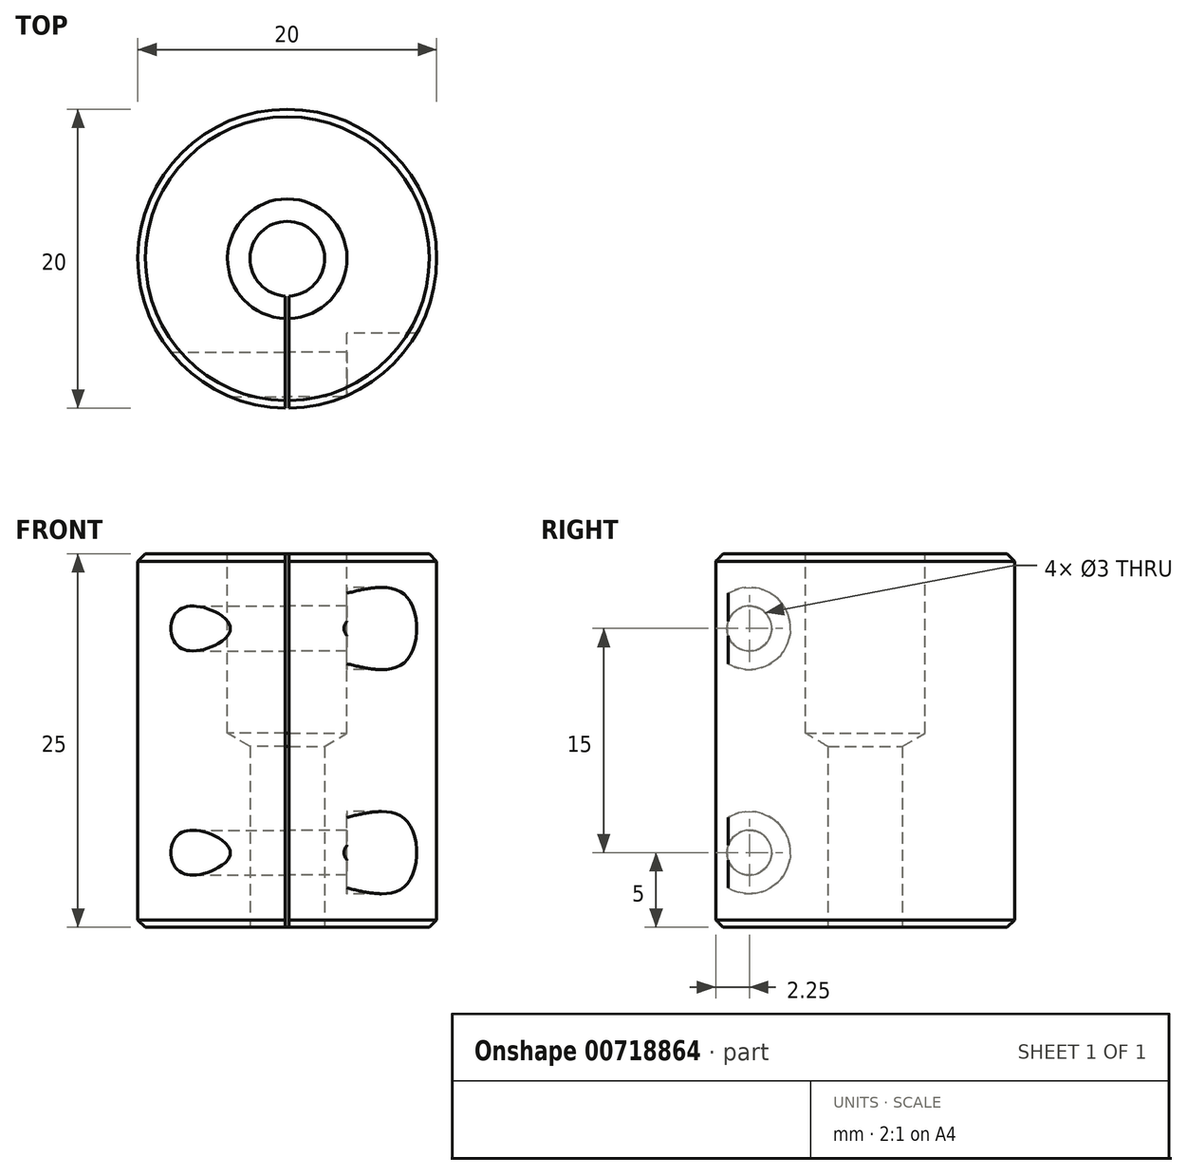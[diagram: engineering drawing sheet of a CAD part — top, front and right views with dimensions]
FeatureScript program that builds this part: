
annotation { "Feature Type Name" : "Feature", "Feature Type Description" : "" }
export const myFeature = defineFeature(function(context is Context, id is Id, definition is map)
    precondition{}
    {
        {
            var Q0;
            Q0=qCreatedBy(makeId("Top.planeOp"),FACE);
            var sketch = newSketch(context, id + "F0", { "sketchPlane" : qUnion([Q0])});
            skCircle(sketch, "E0", {"center": v(0, 0) * mm, "radius": 10 * mm});
            skSolve(sketch);
        }
        {
            var Q0;
            Q0=makeQuery(id+"F0.imprint","IMPRINT",FACE,{"disambiguationData":[TD([[makeQuery(id+"F0.imprint","IMPRINT",EDGE,{"derivedFrom":sQuery(id+"F0.wireOp",EDGE,"E0")}),1.0]])]});
            extrude(context, id + "F1", {"entities" : qUnion([Q0]), "oppositeDirection" : true, "depth" : 25 * mm, "offsetDistance" : 25 * mm});
        }
        {
            var Q0;
            Q0=sQuery(id+"F0.wireOp",VERTEX,"E0.center");
            var Q1;
            Q1=makeQuery(id+"F1.opExtrude","SWEPT_BODY",BODY,{"disambiguationData":[OSD([sQuery(id+"F0.wireOp",EDGE,"E0")])]});
            hole(context, id + "F2", {"style" : HoleStyle.SIMPLE, "endStyle" : HoleEndStyle.BLIND, "holeDiameter" : 8 * mm, "majorDiameter" : 5 * mm, "holeDepth" : 12 * mm, "isTappedThrough" : true, "tappedDepth" : 12 * mm, "tapClearance" : 3, "locations" : qUnion([Q0]), "scope" : qUnion([Q1])});
        }
        {
            var Q0;
            Q0=makeQuery(id+"F1.opExtrude","CAP_FACE",FACE,{"disambiguationData":[OSD([sQuery(id+"F0.wireOp",EDGE,"E0")])],"isStart":false});
            var sketch = newSketch(context, id + "F3", { "sketchPlane" : qUnion([Q0])});
            skCircle(sketch, "E1", {"center": v(0, 0) * mm, "radius": 2.5 * mm});
            skSolve(sketch);
        }
        {
            var Q0;
            Q0 = qSketchRegion(id + "F3", true);
            extrude(context, id + "F4", {"entities" : qUnion([Q0]), "operationType" : NewBodyOperationType.REMOVE, "oppositeDirection" : true, "depth" : 25 * mm, "offsetDistance" : 25 * mm});
        }
        {
            var Q0;
            Q0=qCreatedBy(makeId("Top.planeOp"),FACE);
            var sketch = newSketch(context, id + "F5", { "sketchPlane" : qUnion([Q0])});
            skLineSegment(sketch, "E2.bottom", {"start": v(-0.13, 0) * mm, "end": v(0.13, 0) * mm});
            skLineSegment(sketch, "E2.top", {"start": v(-0.12, -12) * mm, "end": v(0.12, -12) * mm});
            skLineSegment(sketch, "E2.left", {"start": v(-0.13, 0) * mm, "end": v(-0.12, -12) * mm});
            skLineSegment(sketch, "E2.right", {"start": v(0.13, 0) * mm, "end": v(0.12, -12) * mm});
            skSolve(sketch);
        }
        {
            var Q0;
            Q0 = qSketchRegion(id + "F5", true);
            extrude(context, id + "F6", {"entities" : qUnion([Q0]), "operationType" : NewBodyOperationType.REMOVE, "endBound" : BoundingType.THROUGH_ALL, "oppositeDirection" : true, "depth" : 25 * mm, "offsetDistance" : 25 * mm});
        }
        {
            var Q0;
            Q0=makeQuery(id+"F4.boolean.opBoolean","COPY",EDGE,{"derivedFrom":makeQuery(id+"F4.opExtrude","CAP_EDGE",EDGE,{"disambiguationData":[OSD([sQuery(id+"F3.wireOp",EDGE,"E1")])],"isStart":true})});
            var Q1;
            Q1=makeQuery(id+"F1.opExtrude","CAP_EDGE",EDGE,{"disambiguationData":[OSD([sQuery(id+"F0.wireOp",EDGE,"E0")])],"isStart":false});
            var Q2;
            Q2=makeQuery(id+"F1.opExtrude","CAP_EDGE",EDGE,{"disambiguationData":[OSD([sQuery(id+"F0.wireOp",EDGE,"E0")])],"isStart":true});
            var Q3;
            Q3=makeQuery(id+"F2.hole-0.boolean.opBoolean","COPY",EDGE,{"derivedFrom":makeQuery(id+"F2.hole-0.opRevolve","SWEPT_EDGE",EDGE,{"disambiguationData":[OSD([sQuery(id+"F2.hole-0.sketch.wireOp",EDGE,"core_line_2"),sQuery(id+"F2.hole-0.sketch.wireOp",EDGE,"core_line_3")])]})});
            chamfer(context, id + "F7", {"entities" : qUnion([Q0, Q1, Q2, Q3]), "width" : 0.5 * mm, "tangentPropagation" : true});
        }
        {
            var Q0;
            Q0=qCreatedBy(makeId("Right.planeOp"),FACE);
            var sketch = newSketch(context, id + "F8", { "sketchPlane" : qUnion([Q0])});
            skCircle(sketch, "E3", {"center": v(-7.75, -5) * mm, "radius": 1.5 * mm});
            skLineSegment(sketch, "E4", {"start": v(-21.7, -12.5) * mm, "end": v(18.74, -12.5) * mm});
            skCircle(sketch, "E5.MirrorC", {"center": v(-7.75, -20) * mm, "radius": 1.5 * mm});
            skSolve(sketch);
        }
        {
            var Q0;
            Q0=sQuery(id+"F8.wireOp",VERTEX,"E3.center");
            var Q1;
            Q1=sQuery(id+"F8.wireOp",VERTEX,"E5.MirrorC.center");
            var Q2;
            Q2=makeQuery(id+"F1.opExtrude","SWEPT_BODY",BODY,{"disambiguationData":[OSD([sQuery(id+"F0.wireOp",EDGE,"E0")])]});
            hole(context, id + "F9", {"style" : HoleStyle.SIMPLE, "endStyle" : HoleEndStyle.BLIND, "oppositeDirection" : true, "holeDiameter" : 3 * mm, "majorDiameter" : 5 * mm, "holeDepth" : 12 * mm, "isTappedThrough" : true, "tappedDepth" : 12 * mm, "tapClearance" : 3, "locations" : qUnion([Q0, Q1]), "scope" : qUnion([Q2])});
        }
        {
            var Q0;
            Q0 = qSketchRegion(id + "F8", true);
            extrude(context, id + "F10", {"entities" : qUnion([Q0]), "operationType" : NewBodyOperationType.REMOVE, "oppositeDirection" : true, "depth" : 25 * mm, "offsetDistance" : 25 * mm});
        }
        {
            var Q0;
            Q0=qCreatedBy(makeId("Right.planeOp"),FACE);
            cPlane(context, id + "F11", {"entities" : qUnion([Q0]), "cplaneType" : CPlaneType.OFFSET, "offset" : 4 * mm, "width" : 150 * mm, "height" : 150 * mm});
        }
        {
            var Q0;
            Q0=qCreatedBy(id+"F11.planeOp",FACE);
            var sketch = newSketch(context, id + "F12", { "sketchPlane" : qUnion([Q0])});
            skCircle(sketch, "E6", {"center": v(-7.75, -5) * mm, "radius": 2.75 * mm});
            skCircle(sketch, "E7.MirrorC", {"center": v(-7.75, -20) * mm, "radius": 2.75 * mm});
            skSolve(sketch);
        }
        {
            var Q0;
            Q0 = qSketchRegion(id + "F12", true);
            extrude(context, id + "F13", {"entities" : qUnion([Q0]), "operationType" : NewBodyOperationType.REMOVE, "depth" : 25 * mm, "offsetDistance" : 25 * mm});
        }
    });
